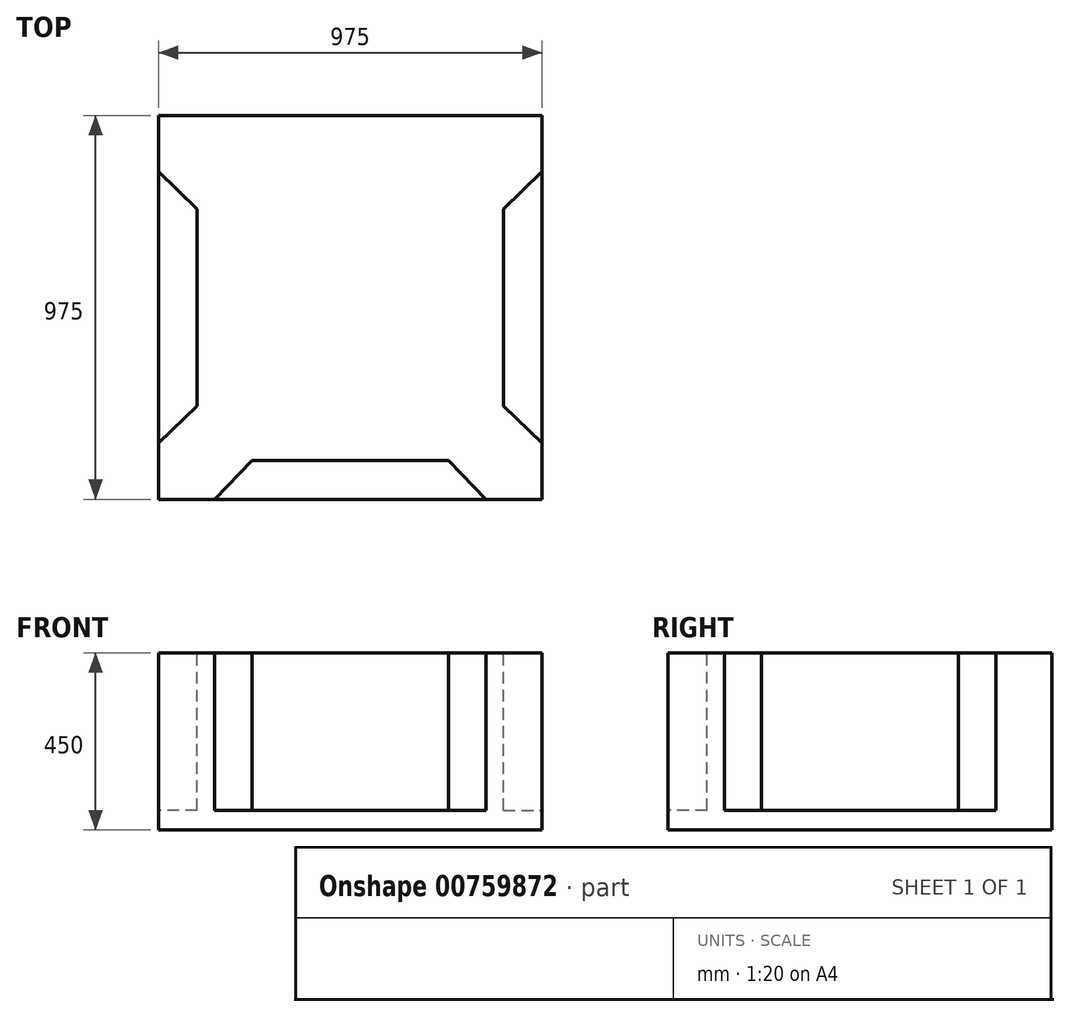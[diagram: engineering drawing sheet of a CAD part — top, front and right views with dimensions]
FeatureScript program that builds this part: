
annotation { "Feature Type Name" : "Feature", "Feature Type Description" : "" }
export const myFeature = defineFeature(function(context is Context, id is Id, definition is map)
    precondition{}
    {
        {
            var Q0;
            Q0=qCreatedBy(makeId("Top.planeOp"),FACE);
            var sketch = newSketch(context, id + "F0", { "sketchPlane" : qUnion([Q0])});
            skLineSegment(sketch, "E0.bottom", {"start": v(300, 300) * mm, "end": v(-300, 300) * mm});
            skLineSegment(sketch, "E0.top", {"start": v(300, -300) * mm, "end": v(-300, -300) * mm});
            skLineSegment(sketch, "E0.left", {"start": v(300, 300) * mm, "end": v(300, -300) * mm});
            skLineSegment(sketch, "E0.right", {"start": v(-300, 300) * mm, "end": v(-300, -300) * mm});
            skPoint(sketch, "E0.middle", {"position": v(0, 0) * mm});
            skLineSegment(sketch, "E1.bottom", {"start": v(487.5, 487.5) * mm, "end": v(-487.5, 487.5) * mm});
            skLineSegment(sketch, "E1.top", {"start": v(487.5, -487.5) * mm, "end": v(-487.5, -487.5) * mm});
            skLineSegment(sketch, "E1.left", {"start": v(487.5, 487.5) * mm, "end": v(487.5, -487.5) * mm});
            skLineSegment(sketch, "E1.right", {"start": v(-487.5, 487.5) * mm, "end": v(-487.5, -487.5) * mm});
            skSolve(sketch);
        }
        {
            var Q0;
            Q0=makeQuery(id+"F0.imprint","IMPRINT",FACE,{"disambiguationData":[TD([[makeQuery(id+"F0.imprint","IMPRINT",EDGE,{"derivedFrom":sQuery(id+"F0.wireOp",EDGE,"E0.bottom")}),-1.0]])]});
            var Q1;
            Q1=makeQuery(id+"F0.imprint","IMPRINT",FACE,{"disambiguationData":[TD([[makeQuery(id+"F0.imprint","IMPRINT",EDGE,{"derivedFrom":sQuery(id+"F0.wireOp",EDGE,"E0.bottom")}),1.0]])]});
            extrude(context, id + "F1", {"entities" : qUnion([Q0, Q1]), "depth" : 450 * mm, "offsetDistance" : 25 * mm});
        }
        {
            var Q0;
            Q0=makeQuery(id+"F1.opExtrude","CAP_FACE",FACE,{"disambiguationData":[OSD([sQuery(id+"F0.wireOp",EDGE,"E1.bottom"),sQuery(id+"F0.wireOp",EDGE,"E1.top"),sQuery(id+"F0.wireOp",EDGE,"E1.left"),sQuery(id+"F0.wireOp",EDGE,"E1.right")])],"isStart":false});
            var sketch = newSketch(context, id + "F2", { "sketchPlane" : qUnion([Q0])});
            skLineSegment(sketch, "E2", {"start": v(-345, 487.5) * mm, "end": v(-250, 388.79) * mm});
            skLineSegment(sketch, "E3", {"start": v(-250, 388.79) * mm, "end": v(250, 388.79) * mm});
            skLineSegment(sketch, "E4", {"start": v(250, 388.79) * mm, "end": v(345, 487.5) * mm});
            skLineSegment(sketch, "E5", {"start": v(345, 487.5) * mm, "end": v(-345, 487.5) * mm});
            skLineSegment(sketch, "E6.1.0", {"start": v(388.79, -250) * mm, "end": v(487.5, -345) * mm});
            skLineSegment(sketch, "E6.1.1", {"start": v(487.5, 345) * mm, "end": v(388.79, 250) * mm});
            skLineSegment(sketch, "E6.1.2", {"start": v(388.79, 250) * mm, "end": v(388.79, -250) * mm});
            skLineSegment(sketch, "E6.1.3", {"start": v(487.5, -345) * mm, "end": v(487.5, 345) * mm});
            skLineSegment(sketch, "E6.2.0", {"start": v(-250, -388.79) * mm, "end": v(-345, -487.5) * mm});
            skLineSegment(sketch, "E6.2.1", {"start": v(345, -487.5) * mm, "end": v(250, -388.79) * mm});
            skLineSegment(sketch, "E6.2.2", {"start": v(250, -388.79) * mm, "end": v(-250, -388.79) * mm});
            skLineSegment(sketch, "E6.2.3", {"start": v(-345, -487.5) * mm, "end": v(345, -487.5) * mm});
            skLineSegment(sketch, "E6.3.0", {"start": v(-388.79, 250) * mm, "end": v(-487.5, 345) * mm});
            skLineSegment(sketch, "E6.3.1", {"start": v(-487.5, -345) * mm, "end": v(-388.79, -250) * mm});
            skLineSegment(sketch, "E6.3.2", {"start": v(-388.79, -250) * mm, "end": v(-388.79, 250) * mm});
            skLineSegment(sketch, "E6.3.3", {"start": v(-487.5, 345) * mm, "end": v(-487.5, -345) * mm});
            skPoint(sketch, "E6.center", {"position": v(0, 0) * mm});
            skLineSegment(sketch, "E6.anchor1", {"start": v(0, 0) * mm, "end": v(-250, 388.79) * mm, "construction": true});
            skLineSegment(sketch, "E6.anchor2", {"start": v(0, 0) * mm, "end": v(-250, 388.79) * mm, "construction": true});
            skSolve(sketch);
        }
        {
            var Q0;
            Q0=makeQuery(id+"F2.imprint","IMPRINT",FACE,{"disambiguationData":[TD([[makeQuery(id+"F2.imprint","IMPRINT",EDGE,{"derivedFrom":sQuery(id+"F2.wireOp",EDGE,"E6.3.0")}),1.0]])]});
            var Q1;
            Q1=makeQuery(id+"F2.imprint","IMPRINT",FACE,{"disambiguationData":[TD([[makeQuery(id+"F2.imprint","IMPRINT",EDGE,{"derivedFrom":sQuery(id+"F2.wireOp",EDGE,"E4")}),1.0]])]});
            var Q2;
            Q2=makeQuery(id+"F2.imprint","IMPRINT",FACE,{"disambiguationData":[TD([[makeQuery(id+"F2.imprint","IMPRINT",EDGE,{"derivedFrom":sQuery(id+"F2.wireOp",EDGE,"E6.1.0")}),1.0]])]});
            var Q3;
            Q3=makeQuery(id+"F2.imprint","IMPRINT",FACE,{"disambiguationData":[TD([[makeQuery(id+"F2.imprint","IMPRINT",EDGE,{"derivedFrom":sQuery(id+"F2.wireOp",EDGE,"E6.2.0")}),1.0]])]});
            extrude(context, id + "F3", {"entities" : qUnion([Q0, Q1, Q2, Q3]), "operationType" : NewBodyOperationType.REMOVE, "oppositeDirection" : true, "depth" : 400 * mm, "offsetDistance" : 25 * mm});
        }
    });
